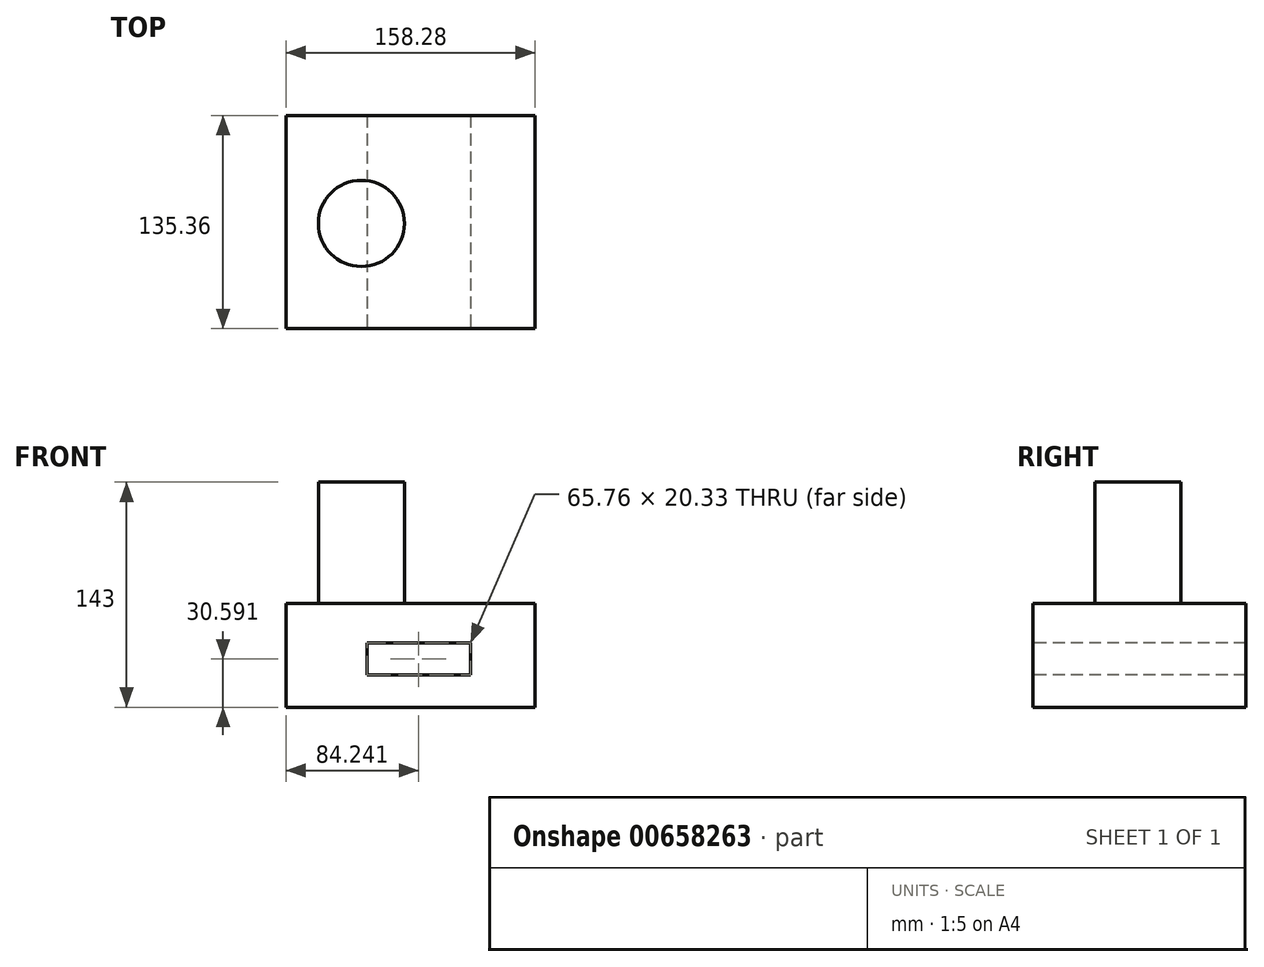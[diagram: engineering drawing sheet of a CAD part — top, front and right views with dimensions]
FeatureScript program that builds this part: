
annotation { "Feature Type Name" : "Feature", "Feature Type Description" : "" }
export const myFeature = defineFeature(function(context is Context, id is Id, definition is map)
    precondition{}
    {
        {
            var Q0;
            Q0=qCreatedBy(makeId("Top.planeOp"),FACE);
            var sketch = newSketch(context, id + "F0", { "sketchPlane" : qUnion([Q0])});
            skLineSegment(sketch, "E0.bottom", {"start": v(0, 0) * mm, "end": v(-158.28, 0) * mm});
            skLineSegment(sketch, "E0.top", {"start": v(0, -135.36) * mm, "end": v(-158.28, -135.36) * mm});
            skLineSegment(sketch, "E0.left", {"start": v(0, 0) * mm, "end": v(0, -135.36) * mm});
            skLineSegment(sketch, "E0.right", {"start": v(-158.28, 0) * mm, "end": v(-158.28, -135.36) * mm});
            skSolve(sketch);
        }
        {
            var Q0;
            Q0=makeQuery(id+"F0.imprint","IMPRINT",FACE,{"disambiguationData":[TD([[makeQuery(id+"F0.imprint","IMPRINT",EDGE,{"derivedFrom":sQuery(id+"F0.wireOp",EDGE,"E0.bottom")}),1.0]])]});
            extrude(context, id + "F1", {"entities" : qUnion([Q0]), "depth" : 66.04 * mm, "offsetDistance" : 25.4 * mm});
        }
        {
            var Q0;
            Q0=makeQuery(id+"F1.opExtrude","CAP_FACE",FACE,{"disambiguationData":[OSD([sQuery(id+"F0.wireOp",EDGE,"E0.bottom"),sQuery(id+"F0.wireOp",EDGE,"E0.top"),sQuery(id+"F0.wireOp",EDGE,"E0.left"),sQuery(id+"F0.wireOp",EDGE,"E0.right")])],"isStart":false});
            var sketch = newSketch(context, id + "F2", { "sketchPlane" : qUnion([Q0])});
            skCircle(sketch, "E1", {"center": v(-110.37, -68.51) * mm, "radius": 27.36 * mm});
            skSolve(sketch);
        }
        {
            var Q0;
            Q0=makeQuery(id+"F2.imprint","IMPRINT",FACE,{"disambiguationData":[TD([[makeQuery(id+"F2.imprint","IMPRINT",EDGE,{"derivedFrom":sQuery(id+"F2.wireOp",EDGE,"E1")}),1.0]])]});
            extrude(context, id + "F3", {"entities" : qUnion([Q0]), "operationType" : NewBodyOperationType.ADD, "depth" : 76.96 * mm, "offsetDistance" : 25.4 * mm});
        }
        {
            var Q0;
            Q0=makeQuery(id+"F1.opExtrude","SWEPT_FACE",FACE,{"disambiguationData":[OSD([sQuery(id+"F0.wireOp",EDGE,"E0.top")])]});
            var sketch = newSketch(context, id + "F4", { "sketchPlane" : qUnion([Q0])});
            skLineSegment(sketch, "E2.bottom", {"start": v(-106.92, 40.76) * mm, "end": v(-41.16, 40.76) * mm});
            skLineSegment(sketch, "E2.top", {"start": v(-106.92, 20.42) * mm, "end": v(-41.16, 20.42) * mm});
            skLineSegment(sketch, "E2.left", {"start": v(-106.92, 40.76) * mm, "end": v(-106.92, 20.42) * mm});
            skLineSegment(sketch, "E2.right", {"start": v(-41.16, 40.76) * mm, "end": v(-41.16, 20.42) * mm});
            skSolve(sketch);
        }
        {
            var Q0;
            Q0=makeQuery(id+"F4.imprint","IMPRINT",FACE,{"disambiguationData":[TD([[makeQuery(id+"F4.imprint","IMPRINT",EDGE,{"derivedFrom":sQuery(id+"F4.wireOp",EDGE,"E2.bottom")}),-1.0]])]});
            extrude(context, id + "F5", {"entities" : qUnion([Q0]), "operationType" : NewBodyOperationType.REMOVE, "oppositeDirection" : true, "depth" : 178.3 * mm, "offsetDistance" : 25.4 * mm});
        }
    });
